# Revit family: Wall_mount-ada_cooler-elkay-LZO8L
name_source: partatom
category: Plumbing Fixtures
units: mm (PartAtom-declared; Revit-internal decimal feet)

## family parameters
Always vertical = Yes
Cut with Voids When Loaded = No
Maintain Annotation Orientation = No
OmniClass Number = 23.65.70.14.11
OmniClass Title = Drinking Fountains/Coolers
Part Type = Normal
Room Calculation Point = No
Round Connector Dimension = Use Diameter
Shared = No
Work Plane-Based = No

## types (1)
- LZO8L (Hands-free Activation Wall Mount ADA Cooler)
    Activation Method = Electronic Sensor Bubbler
    Approx. Shipping Weight (lbs) = 54
    Assembly Code = D2010.60
    Chilling Capacity(GPH) = 8
    Connector Outlet B = 1 1/4"
    Connector Supply A = 1/2"
    Current = 0 A
    Default Elevation = 0"
    Description = Wall Mount Hands-free Activation ADA Cooler Filtered Refrigerated Light Gray Granite
    Dimensions (L x W x H) = "18 3/8 inch x 19 inch x 19 13/16 inch"
    Inlet Connection Size (inch) = 1/2"
    Installation Location = Indoor
    Main Material = Finish-Elkay-Steel
    Manufacturer = Elkay Manufacturer Company
    Manufacturer Brand = Elkay (by Zurn Elkay Water Solutions)
    Masking A1 = 21 1/2"
    Masking A2 = 21"
    Masking Arc Radius = 21"
    Material_Shroud = Finish-Elkay-Light Gray
    Material_Wrapper = Finish-Elkay-Light Gray(1)
    Model = LZO8L
    Mounting Type = Wall Mount (On Wall)
    Number of Poles = 1
    Outlet Connection Size (inch) = 1.25
    Power Factor = 1
    Product Documentation Link = https://www.elkayfiles.com
    Product Installation Sheet URL = https://www.elkayfiles.com
    Product Page URL = https://www.elkay.com
    Product Weight (lbs) = 19
    Product data URL = https://bimobject.com
    Repair Parts URL = https://www.elkayfiles.com
    URL = https://www.elkay.com
    Voltage = 115 V
    sensor button = 0"

## geometry (parser evidence)
native form markers: Sweep x8
no freeform markers — native parametric forms only
